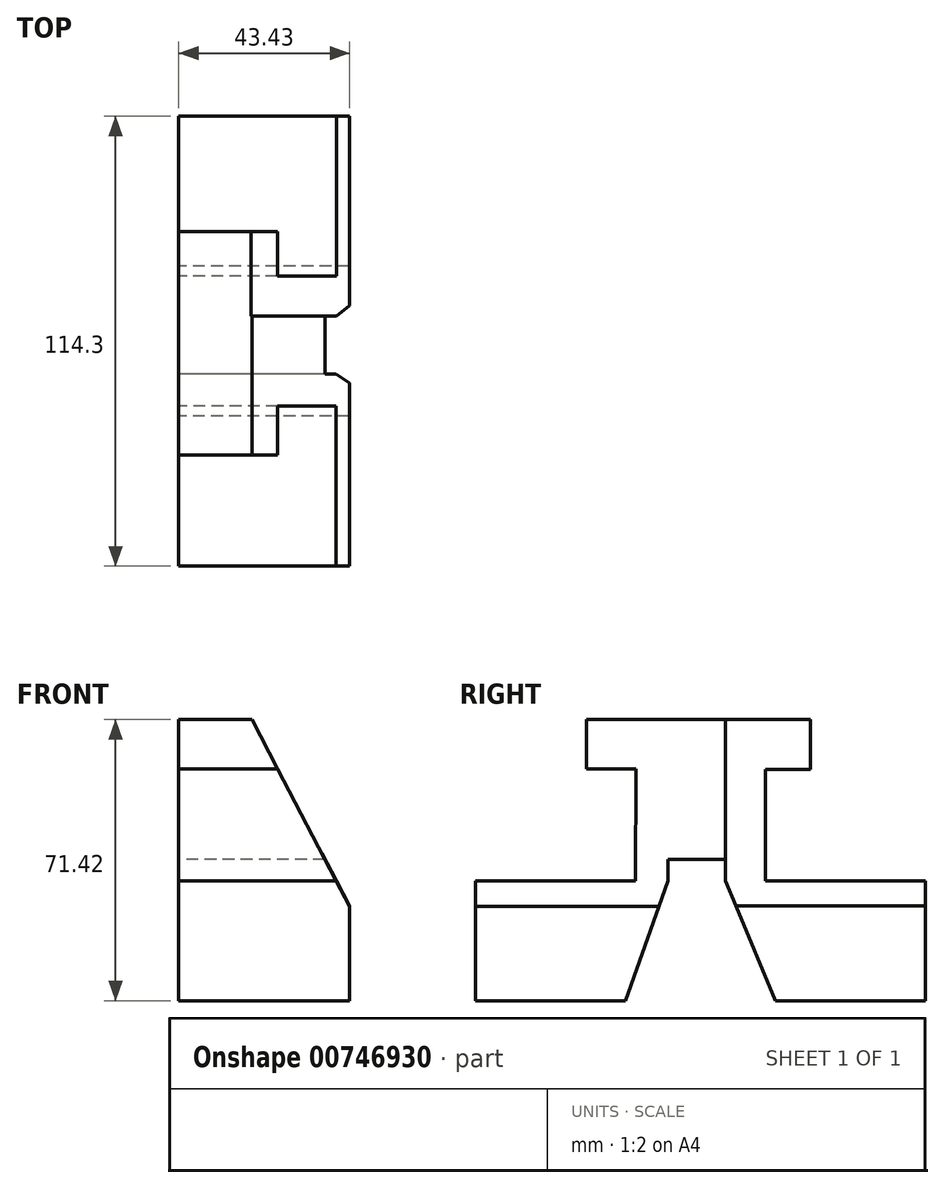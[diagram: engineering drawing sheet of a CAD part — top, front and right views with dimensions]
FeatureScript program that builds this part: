
annotation { "Feature Type Name" : "Feature", "Feature Type Description" : "" }
export const myFeature = defineFeature(function(context is Context, id is Id, definition is map)
    precondition{}
    {
        {
            var Q0;
            Q0=qCreatedBy(makeId("Right.planeOp"),FACE);
            var sketch = newSketch(context, id + "F0", { "sketchPlane" : qUnion([Q0])});
            skLineSegment(sketch, "E0", {"start": v(-35.33, 40.94) * mm, "end": v(21.55, 40.94) * mm});
            skLineSegment(sketch, "E1", {"start": v(21.55, 28.31) * mm, "end": v(21.55, 40.94) * mm});
            skLineSegment(sketch, "E2", {"start": v(21.55, 28.31) * mm, "end": v(10.16, 28.31) * mm});
            skLineSegment(sketch, "E3", {"start": v(10.16, 28.31) * mm, "end": v(10.16, 0) * mm});
            skLineSegment(sketch, "E4", {"start": v(10.16, 0) * mm, "end": v(50.8, 0) * mm});
            skLineSegment(sketch, "E5", {"start": v(50.8, 0) * mm, "end": v(50.8, -30.48) * mm});
            skLineSegment(sketch, "E6", {"start": v(50.8, -30.48) * mm, "end": v(12.7, -30.48) * mm});
            skLineSegment(sketch, "E7", {"start": v(12.7, -30.48) * mm, "end": v(0, 0) * mm});
            skLineSegment(sketch, "E8", {"start": v(0, 0) * mm, "end": v(0, 5.44) * mm});
            skLineSegment(sketch, "E9", {"start": v(0, 5.44) * mm, "end": v(-14.67, 5.44) * mm});
            skLineSegment(sketch, "E10", {"start": v(-14.67, 5.44) * mm, "end": v(-14.67, 0) * mm});
            skLineSegment(sketch, "E11", {"start": v(-14.67, 0) * mm, "end": v(-25.4, -30.48) * mm});
            skLineSegment(sketch, "E12", {"start": v(-25.4, -30.48) * mm, "end": v(-63.5, -30.48) * mm});
            skLineSegment(sketch, "E13", {"start": v(-63.5, -30.48) * mm, "end": v(-63.5, 0) * mm});
            skLineSegment(sketch, "E14", {"start": v(-63.5, 0) * mm, "end": v(-22.86, 0) * mm});
            skLineSegment(sketch, "E15", {"start": v(-22.86, 0) * mm, "end": v(-22.82, 28.43) * mm});
            skLineSegment(sketch, "E16", {"start": v(-22.82, 28.43) * mm, "end": v(-35.33, 28.43) * mm});
            skLineSegment(sketch, "E17", {"start": v(-35.33, 28.43) * mm, "end": v(-35.33, 40.94) * mm});
            skSolve(sketch);
        }
        {
            var Q0;
            Q0 = qSketchRegion(id + "F0", true);
            extrude(context, id + "F1", {"entities" : qUnion([Q0]), "depth" : 43.43 * mm, "offsetDistance" : 25.4 * mm});
        }
        {
            var Q0;
            Q0=qCreatedBy(makeId("Front.planeOp"),FACE);
            var sketch = newSketch(context, id + "F2", { "sketchPlane" : qUnion([Q0])});
            skLineSegment(sketch, "E18", {"start": v(45.27, -9.9) * mm, "end": v(45.27, 47.28) * mm});
            skLineSegment(sketch, "E19", {"start": v(45.27, 47.28) * mm, "end": v(15.07, 47.28) * mm});
            skLineSegment(sketch, "E20", {"start": v(15.07, 47.28) * mm, "end": v(45.27, -9.9) * mm});
            skSolve(sketch);
        }
        {
            var Q0;
            Q0 = qSketchRegion(id + "F2", true);
            extrude(context, id + "F3", {"entities" : qUnion([Q0]), "operationType" : NewBodyOperationType.REMOVE, "oppositeDirection" : true, "depth" : 57.4 * mm, "offsetDistance" : 25.4 * mm});
        }
        {
            var Q0;
            Q0=qCreatedBy(makeId("Front.planeOp"),FACE);
            var sketch = newSketch(context, id + "F4", { "sketchPlane" : qUnion([Q0])});
            skLineSegment(sketch, "E21", {"start": v(45.16, -9.87) * mm, "end": v(45.16, 42.4) * mm});
            skLineSegment(sketch, "E22", {"start": v(45.16, 42.4) * mm, "end": v(17.86, 42.4) * mm});
            skLineSegment(sketch, "E23", {"start": v(17.86, 42.4) * mm, "end": v(45.16, -9.87) * mm});
            skSolve(sketch);
        }
        {
            var Q0;
            Q0 = qSketchRegion(id + "F4", true);
            extrude(context, id + "F5", {"entities" : qUnion([Q0]), "operationType" : NewBodyOperationType.REMOVE, "depth" : 71.63 * mm, "offsetDistance" : 25.4 * mm});
        }
    });
